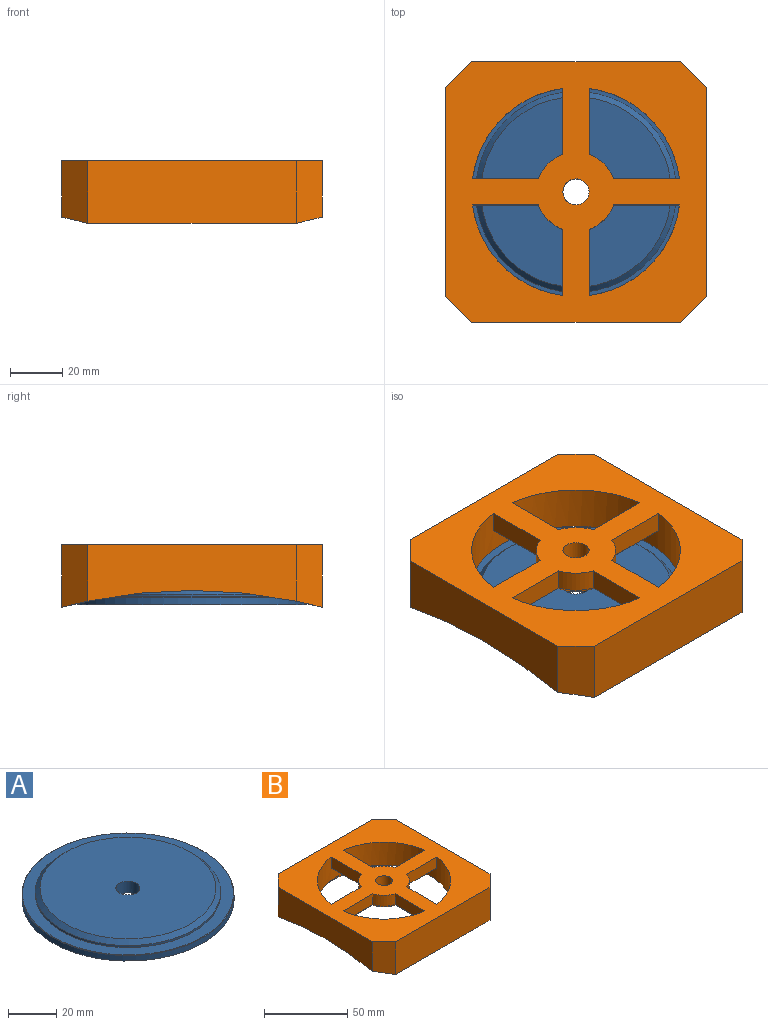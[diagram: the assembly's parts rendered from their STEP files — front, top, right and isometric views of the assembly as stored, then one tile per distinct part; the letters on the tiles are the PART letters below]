
ASSEMBLY  parts=2 mates=1
PART A: 8 faces, bbox 88x88x6 mm
  f0: cylinder r=44mm len=88mm, axis (0,0,1), area 774.1mm2, adj f1,f6
  f1: plane 88x88mm, normal (0,0,-1), area 6003.6mm2, adj f0,f7
  f2: plane 87.6x87.6mm, normal (0,0,1), area 1370.3mm2, adj f3,f6
  f3: cylinder r=38.5mm len=77mm, axis (0,0,-1), area 241.9mm2, adj f2,f5
  f4: plane 73x73mm, normal (0,0,1), area 4106.8mm2, adj f5,f7
  f5: cone r=36.5mm half-angle=45deg, axis (0,0,-1), area 666.4mm2, adj f3,f4
  f6: cone r=44mm half-angle=45deg, axis (0,0,-1), area 78mm2, adj f0,f2
  f7: cylinder r=5mm len=10mm, axis (0,0,1), area 188.5mm2, adj f1,f4
PART B: 39 faces, bbox 100x100x24.1 mm
  f0: plane 90x90mm, normal (0,0,-1), area 1335.2mm2, adj f4,f33
  f1: plane 80x24.1mm, normal (0,1,0), area 1928mm2, adj f6,f34,f35,f38
  f2: plane 80x21.73mm, normal (-1,0,0), area 1516.6mm2, adj f6,f34,f35,f36
  f3: plane 80x24.1mm, normal (0,-1,0), area 1928mm2, adj f6,f34,f36,f37
  f4: cylinder r=40mm len=80mm, axis (0,0,-1), area 3887.6mm2, adj f0,f6,f7,f8,f10,f11,f13,f14
  f5: plane 80x21.73mm, normal (1,0,0), area 1516.6mm2, adj f6,f34,f37,f38
  f6: plane 100x100mm, normal (0,0,1), area 6419.8mm2, adj f1,f2,f3,f4,f5,f7,f8,f9
  f7: plane 25.33x8mm, normal (-1,0,0), area 202.6mm2, adj f4,f6,f18,f29
  f8: plane 25.33x8mm, normal (1,0,0), area 202.6mm2, adj f4,f6,f9,f24
  f9: cylinder r=15.2mm len=9.36mm, axis (0,0,1), area 109.5mm2, adj f6,f8,f10,f25
  f10: plane 25.33x8mm, normal (0,-1,0), area 202.6mm2, adj f4,f6,f9,f26
  f11: plane 25.33x8mm, normal (0,1,0), area 202.6mm2, adj f4,f6,f12,f21
  f12: cylinder r=15.2mm len=9.36mm, axis (0,0,1), area 109.5mm2, adj f6,f11,f13,f22
  f13: plane 25.33x8mm, normal (1,0,0), area 202.6mm2, adj f4,f6,f12,f23
  f14: plane 25.33x8mm, normal (-1,0,0), area 202.6mm2, adj f4,f6,f15,f30
  f15: cylinder r=15.2mm len=9.36mm, axis (0,0,1), area 109.5mm2, adj f6,f14,f16,f31
  f16: plane 25.33x8mm, normal (0,1,0), area 202.6mm2, adj f4,f6,f15,f32
  f17: plane 25.33x8mm, normal (0,-1,0), area 202.6mm2, adj f4,f6,f18,f27
  f18: cylinder r=15.2mm len=9.36mm, axis (0,0,1), area 109.5mm2, adj f6,f7,f17,f28
  f19: cylinder r=5mm len=10mm, axis (0,0,1), area 314.2mm2, adj f6,f20
  f20: plane 80x80mm, normal (0,0,-1), area 1114mm2, adj f4,f19,f21,f22,f23,f24,f25,f26
  f21: plane 27.03x2mm, normal (0,0.71,-0.71), area 74mm2, adj f4,f11,f20,f22
  f22: cone r=15.2mm half-angle=45deg, axis (0,0,1), area 40.2mm2, adj f12,f20,f21,f23
  f23: plane 27.03x2mm, normal (0.71,0,-0.71), area 74mm2, adj f4,f13,f20,f22
  f24: plane 27.03x2mm, normal (0.71,0,-0.71), area 74mm2, adj f4,f8,f20,f25
  f25: cone r=15.2mm half-angle=45deg, axis (0,0,1), area 40.2mm2, adj f9,f20,f24,f26
  f26: plane 27.03x2mm, normal (0,-0.71,-0.71), area 74mm2, adj f4,f10,f20,f25
  f27: plane 27.03x2mm, normal (0,-0.71,-0.71), area 74mm2, adj f4,f17,f20,f28
  f28: cone r=15.2mm half-angle=45deg, axis (0,0,1), area 40.2mm2, adj f18,f20,f27,f29
  f29: plane 27.03x2mm, normal (-0.71,0,-0.71), area 74mm2, adj f4,f7,f20,f28
  f30: plane 27.03x2mm, normal (-0.71,0,-0.71), area 74mm2, adj f4,f14,f20,f31
  f31: cone r=15.2mm half-angle=45deg, axis (0,0,1), area 40.2mm2, adj f15,f20,f30,f32
  f32: plane 27.03x2mm, normal (0,0.71,-0.71), area 74mm2, adj f4,f16,f20,f31
  f33: cylinder r=45mm len=90mm, axis (0,0,1), area 906.8mm2, adj f0,f34
  f34: cylinder r=195mm len=100mm, axis (1,0,0), area 3504.1mm2, adj f1,f2,f3,f5,f33,f35,f36,f37
  f35: plane 24.13x10.03mm, normal (-0.71,0.71,0), area 323.4mm2, adj f1,f2,f6,f34
  f36: plane 24.13x10.03mm, normal (-0.71,-0.71,0), area 323.4mm2, adj f2,f3,f6,f34
  f37: plane 24.13x10.03mm, normal (0.71,-0.71,0), area 323.4mm2, adj f3,f5,f6,f34
  f38: plane 24.13x10.03mm, normal (0.71,0.71,0), area 323.4mm2, adj f1,f5,f6,f34
PLACE A t=(0,0,46)mm
PLACE B at identity
MATE slider A.f0 <-> B.f4  axis (0,0,1) through (18.31,12.09,0)mm
